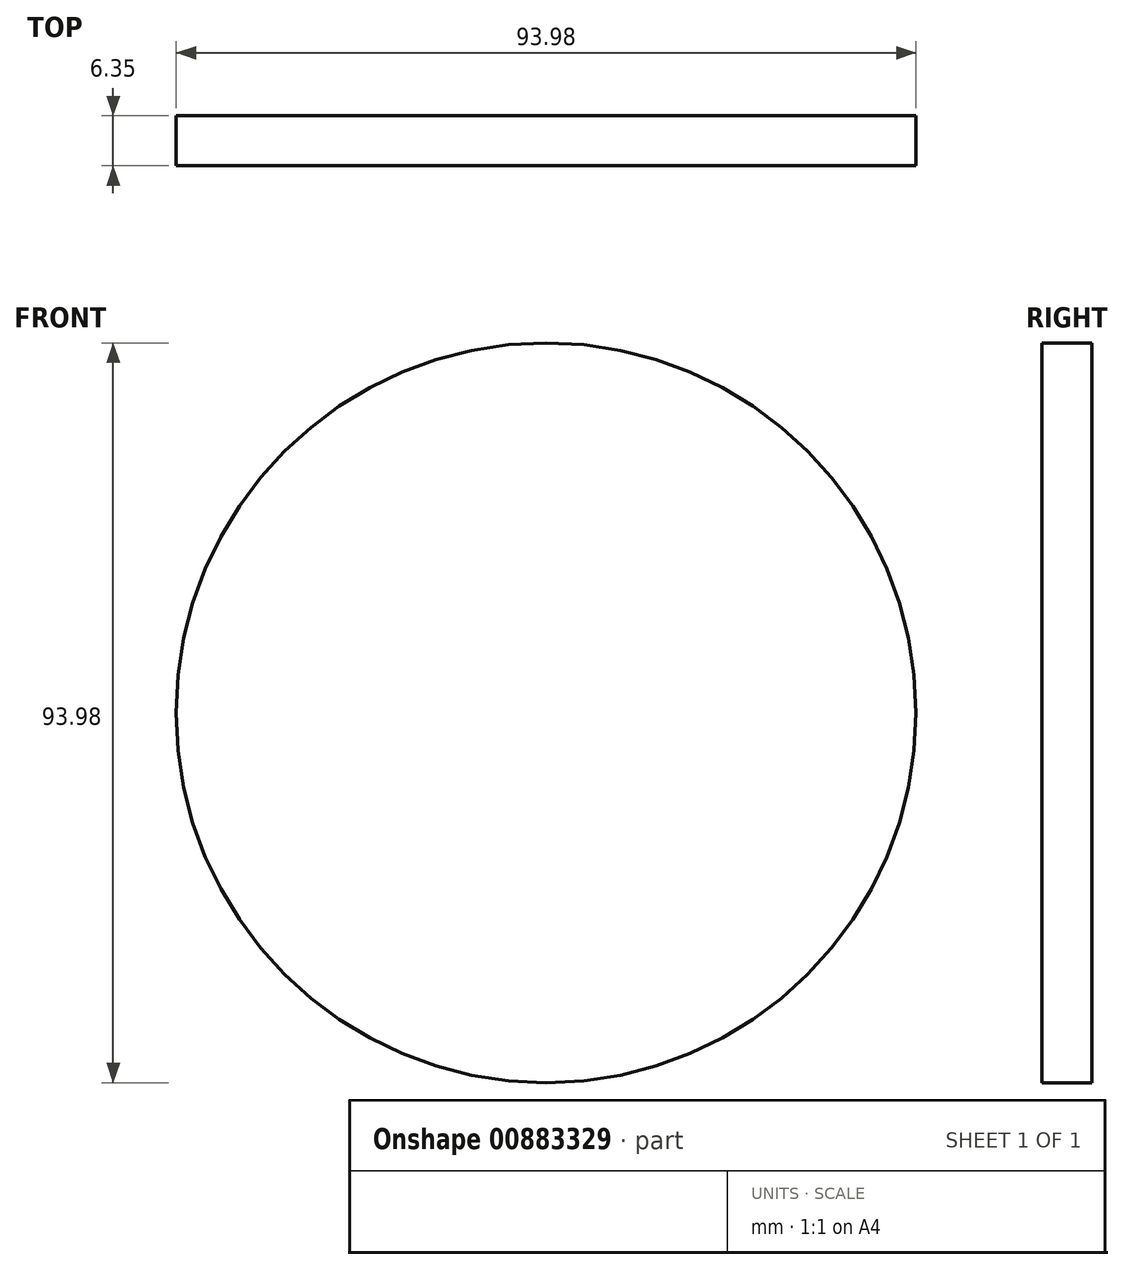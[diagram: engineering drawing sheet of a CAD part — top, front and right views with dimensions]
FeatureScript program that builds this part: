
annotation { "Feature Type Name" : "Feature", "Feature Type Description" : "" }
export const myFeature = defineFeature(function(context is Context, id is Id, definition is map)
    precondition{}
    {
        {
            var Q0;
            Q0=qCreatedBy(makeId("Front.planeOp"),FACE);
            var sketch = newSketch(context, id + "F0", { "sketchPlane" : qUnion([Q0])});
            skCircle(sketch, "E0", {"center": v(0, 0) * mm, "radius": 47 * mm});
            skSolve(sketch);
        }
        {
            var Q0;
            Q0=makeQuery(id+"F0.imprint","IMPRINT",FACE,{"disambiguationData":[TD([[makeQuery(id+"F0.imprint","IMPRINT",EDGE,{"derivedFrom":sQuery(id+"F0.wireOp",EDGE,"E0")}),1.0]])]});
            extrude(context, id + "F1", {"entities" : qUnion([Q0]), "depth" : 6.35 * mm, "offsetDistance" : 25.4 * mm});
        }
    });
